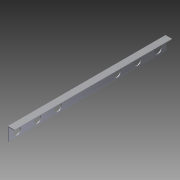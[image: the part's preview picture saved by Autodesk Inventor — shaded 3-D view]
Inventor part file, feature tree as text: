
AUTODESK INVENTOR PART (.ipt)
format: ipt  version: 2012 (Build 160160000, 160)  size: 96,768 bytes
history: native  units: in
note: dims shown in document units (in); Inventor stores cm internally (conversion verified against a paired STEP export)
features: extrude x2, sketch x2
ambient origin geometry x8: Origin, YZ Plane, XZ Plane, XY Plane, X Axis, Y Axis, Z Axis, Center Point
bodies: Solid1 (feature_tree)
feature tree (4):
  extrude  "Extrusion1"  Depth=1.0in
  extrude  "Extrusion2"  Depth=0.125in
  sketch  "Sketch1"  dims[d0=2.0in d1=1.0in]
  sketch  "Sketch2"  dims[d2=0.125in d3=0.125in d4=24.0in d5=0.0in d6=1.125in d7=1.25in d8=0.75in d9=1.125in d10=9.0in d11=1.25in d13=24.25in d14=0.0in d15=6.25in d16=3.125in d17=3.125in d18=24.0in]
